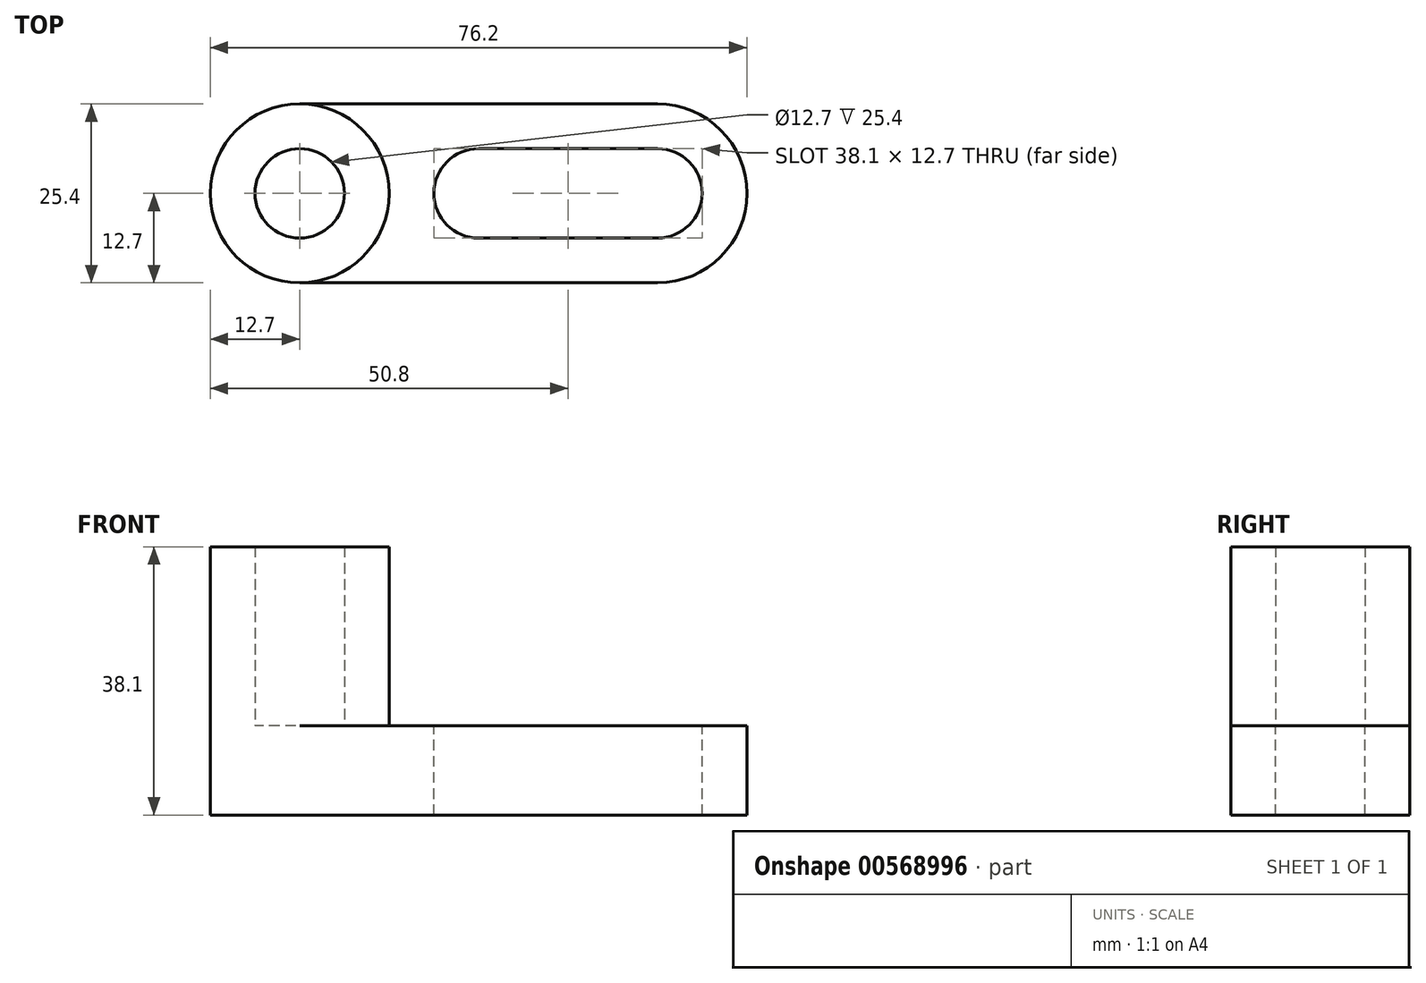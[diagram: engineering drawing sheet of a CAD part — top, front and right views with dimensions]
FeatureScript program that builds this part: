
annotation { "Feature Type Name" : "Feature", "Feature Type Description" : "" }
export const myFeature = defineFeature(function(context is Context, id is Id, definition is map)
    precondition{}
    {
        {
            var Q0;
            Q0=qCreatedBy(makeId("Front.planeOp"),FACE);
            var sketch = newSketch(context, id + "F0", { "sketchPlane" : qUnion([Q0])});
            skLineSegment(sketch, "E0", {"start": v(0, 0) * mm, "end": v(76.2, 0) * mm});
            skLineSegment(sketch, "E1", {"start": v(76.2, 0) * mm, "end": v(76.2, 12.7) * mm});
            skLineSegment(sketch, "E2", {"start": v(76.2, 12.7) * mm, "end": v(0, 12.7) * mm});
            skLineSegment(sketch, "E3", {"start": v(0, 12.7) * mm, "end": v(0, 0) * mm});
            skSolve(sketch);
        }
        {
            var Q0;
            Q0=makeQuery(id+"F0.imprint","IMPRINT",FACE,{"disambiguationData":[TD([[makeQuery(id+"F0.imprint","IMPRINT",EDGE,{"derivedFrom":sQuery(id+"F0.wireOp",EDGE,"E0")}),1.0]])]});
            extrude(context, id + "F1", {"entities" : qUnion([Q0]), "depth" : 25.4 * mm, "offsetDistance" : 25.4 * mm});
        }
        {
            var Q0;
            Q0=makeQuery(id+"F1.opExtrude","SWEPT_FACE",FACE,{"disambiguationData":[OSD([sQuery(id+"F0.wireOp",EDGE,"E2")])]});
            var sketch = newSketch(context, id + "F2", { "sketchPlane" : qUnion([Q0])});
            skCircle(sketch, "E4", {"center": v(63.5, -12.7) * mm, "radius": 6.35 * mm});
            skCircle(sketch, "E5", {"center": v(38.1, -12.7) * mm, "radius": 6.35 * mm});
            skLineSegment(sketch, "E6", {"start": v(38.1, -6.35) * mm, "end": v(63.5, -6.35) * mm});
            skLineSegment(sketch, "E7", {"start": v(63.5, -6.35) * mm, "end": v(63.5, -19.05) * mm});
            skLineSegment(sketch, "E8", {"start": v(63.5, -19.05) * mm, "end": v(38.1, -19.05) * mm});
            skLineSegment(sketch, "E9", {"start": v(38.1, -19.05) * mm, "end": v(38.1, -6.35) * mm});
            skLineSegment(sketch, "E10", {"start": v(63.5, 0) * mm, "end": v(63.5, -25.4) * mm});
            skArc(sketch, "E11", {"start": v(63.5, -25.4) * mm, "mid": v(76.2, -12.7) * mm, "end": v(63.5, 0) * mm});
            skPoint(sketch, "E12.startSnap0", {"position": v(0, -12.7) * mm});
            skLineSegment(sketch, "E13", {"start": v(12.7, -12.7) * mm, "end": v(38.1, -12.7) * mm});
            skArc(sketch, "E14", {"start": v(12.7, 0) * mm, "mid": v(0, -12.7) * mm, "end": v(12.7, -25.4) * mm});
            skSolve(sketch);
        }
        {
            var Q0;
            {var subQ0=sQuery(id+"F2.wireOp",EDGE,"E14");var subQ1=sQuery(id+"F0.wireOp",EDGE,"E2");var subQ2=makeQuery(id+"F1.opExtrude","CAP_EDGE",EDGE,{"disambiguationData":[OSD([subQ1])],"isStart":false});var subQ3=makeQuery(id+"F2.imprint","INTERSECT",VERTEX,{"derivedFrom":[subQ2,subQ0]});Q0=makeQuery(id+"F2.imprint","IMPRINT",FACE,{"disambiguationData":[TD([[makeQuery(id+"F2.imprint","IMPRINT",EDGE,{"disambiguationData":[TD([[subQ3,1.0]])],"derivedFrom":subQ0}),-1.0]])]});}
            var Q1;
            {var subQ0=sQuery(id+"F2.wireOp",EDGE,"E14");var subQ1=sQuery(id+"F0.wireOp",EDGE,"E2");var subQ2=makeQuery(id+"F1.opExtrude","CAP_EDGE",EDGE,{"disambiguationData":[OSD([subQ1])],"isStart":true});var subQ3=makeQuery(id+"F2.imprint","INTERSECT",VERTEX,{"derivedFrom":[subQ2,subQ0]});Q1=makeQuery(id+"F2.imprint","IMPRINT",FACE,{"disambiguationData":[TD([[makeQuery(id+"F2.imprint","IMPRINT",EDGE,{"disambiguationData":[TD([[subQ3,-1.0]])],"derivedFrom":subQ0}),-1.0]])]});}
            var Q2;
            {var subQ1=sQuery(id+"F2.wireOp",EDGE,"E6");Q2=makeQuery(id+"F2.imprint","IMPRINT",FACE,{"disambiguationData":[TD([[makeQuery(id+"F2.imprint","IMPRINT",EDGE,{"derivedFrom":subQ1}),-1.0]])]});}
            var Q3;
            {var subQ0=sQuery(id+"F2.wireOp",EDGE,"E9");var subQ3=sQuery(id+"F2.wireOp",EDGE,"E13");var subQ5=makeQuery(id+"F2.imprint","INTERSECT",VERTEX,{"derivedFrom":[subQ0,subQ3]});Q3=makeQuery(id+"F2.imprint","IMPRINT",FACE,{"disambiguationData":[TD([[makeQuery(id+"F2.imprint","IMPRINT",EDGE,{"disambiguationData":[TD([[subQ5,1.0]])],"derivedFrom":subQ3}),1.0]])]});}
            var Q4;
            {var subQ0=sQuery(id+"F2.wireOp",EDGE,"E9");var subQ3=sQuery(id+"F2.wireOp",EDGE,"E13");var subQ5=makeQuery(id+"F2.imprint","INTERSECT",VERTEX,{"derivedFrom":[subQ0,subQ3]});Q4=makeQuery(id+"F2.imprint","IMPRINT",FACE,{"disambiguationData":[TD([[makeQuery(id+"F2.imprint","IMPRINT",EDGE,{"disambiguationData":[TD([[subQ5,1.0]])],"derivedFrom":subQ3}),-1.0]])]});}
            var Q5;
            {var subQ0=sQuery(id+"F2.wireOp",EDGE,"E9");var subQ4=makeQuery(id+"F2.imprint","INTERSECT",VERTEX,{"derivedFrom":[subQ0,sQuery(id+"F2.wireOp",EDGE,"E13")]});Q5=makeQuery(id+"F2.imprint","IMPRINT",FACE,{"disambiguationData":[TD([[makeQuery(id+"F2.imprint","IMPRINT",EDGE,{"disambiguationData":[TD([[subQ4,1.0]])],"derivedFrom":subQ0}),-1.0]])]});}
            var Q6;
            {var subQ0=sQuery(id+"F2.wireOp",EDGE,"E10");var subQ1=sQuery(id+"F2.wireOp",EDGE,"E4");var subQ2=makeQuery(id+"F2.imprint","INTERSECT",VERTEX,{"derivedFrom":[subQ1,sQuery(id+"F2.wireOp",EDGE,"E6"),subQ0]});Q6=makeQuery(id+"F2.imprint","IMPRINT",FACE,{"disambiguationData":[TD([[makeQuery(id+"F2.imprint","IMPRINT",EDGE,{"disambiguationData":[TD([[subQ2,-1.0]])],"derivedFrom":subQ1}),1.0]])]});}
            var Q7;
            {var subQ0=sQuery(id+"F2.wireOp",EDGE,"E10");var subQ1=sQuery(id+"F2.wireOp",EDGE,"E4");var subQ2=makeQuery(id+"F2.imprint","INTERSECT",VERTEX,{"derivedFrom":[subQ1,sQuery(id+"F2.wireOp",EDGE,"E6"),subQ0]});Q7=makeQuery(id+"F2.imprint","IMPRINT",FACE,{"disambiguationData":[TD([[makeQuery(id+"F2.imprint","IMPRINT",EDGE,{"disambiguationData":[TD([[subQ2,1.0]])],"derivedFrom":subQ1}),1.0]])]});}
            var Q8;
            {var subQ0=sQuery(id+"F2.wireOp",EDGE,"E11");var subQ1=sQuery(id+"F0.wireOp",EDGE,"E2");var subQ2=makeQuery(id+"F1.opExtrude","CAP_EDGE",EDGE,{"disambiguationData":[OSD([subQ1])],"isStart":true});var subQ3=makeQuery(id+"F2.imprint","INTERSECT",VERTEX,{"derivedFrom":[subQ2,sQuery(id+"F2.wireOp",EDGE,"E10"),subQ0]});Q8=makeQuery(id+"F2.imprint","IMPRINT",FACE,{"disambiguationData":[TD([[makeQuery(id+"F2.imprint","IMPRINT",EDGE,{"disambiguationData":[TD([[subQ3,1.0]])],"derivedFrom":subQ0}),-1.0]])]});}
            var Q9;
            {var subQ0=sQuery(id+"F2.wireOp",EDGE,"E11");var subQ1=sQuery(id+"F0.wireOp",EDGE,"E2");var subQ2=makeQuery(id+"F1.opExtrude","CAP_EDGE",EDGE,{"disambiguationData":[OSD([subQ1])],"isStart":false});var subQ3=makeQuery(id+"F2.imprint","INTERSECT",VERTEX,{"derivedFrom":[subQ2,sQuery(id+"F2.wireOp",EDGE,"E10"),subQ0]});Q9=makeQuery(id+"F2.imprint","IMPRINT",FACE,{"disambiguationData":[TD([[makeQuery(id+"F2.imprint","IMPRINT",EDGE,{"disambiguationData":[TD([[subQ3,-1.0]])],"derivedFrom":subQ0}),-1.0]])]});}
            extrude(context, id + "F3", {"entities" : qUnion([Q0, Q1, Q2, Q3, Q4, Q5, Q6, Q7, Q8, Q9]), "operationType" : NewBodyOperationType.REMOVE, "oppositeDirection" : true, "depth" : 12.7 * mm, "offsetDistance" : 25.4 * mm});
        }
        {
            var Q0;
            Q0=makeQuery(id+"F1.opExtrude","SWEPT_FACE",FACE,{"disambiguationData":[OSD([sQuery(id+"F0.wireOp",EDGE,"E2")])]});
            var sketch = newSketch(context, id + "F4", { "sketchPlane" : qUnion([Q0])});
            skCircle(sketch, "E15", {"center": v(12.7, -12.7) * mm, "radius": 12.7 * mm});
            skCircle(sketch, "E16", {"center": v(12.7, -12.7) * mm, "radius": 6.35 * mm});
            skSolve(sketch);
        }
        {
            var Q0;
            Q0=makeQuery(id+"F4.imprint","IMPRINT",FACE,{"disambiguationData":[TD([[makeQuery(id+"F4.imprint","IMPRINT",EDGE,{"derivedFrom":sQuery(id+"F4.wireOp",EDGE,"E16")}),-1.0]])]});
            extrude(context, id + "F5", {"entities" : qUnion([Q0]), "operationType" : NewBodyOperationType.ADD, "depth" : 25.4 * mm, "offsetDistance" : 25.4 * mm});
        }
    });
